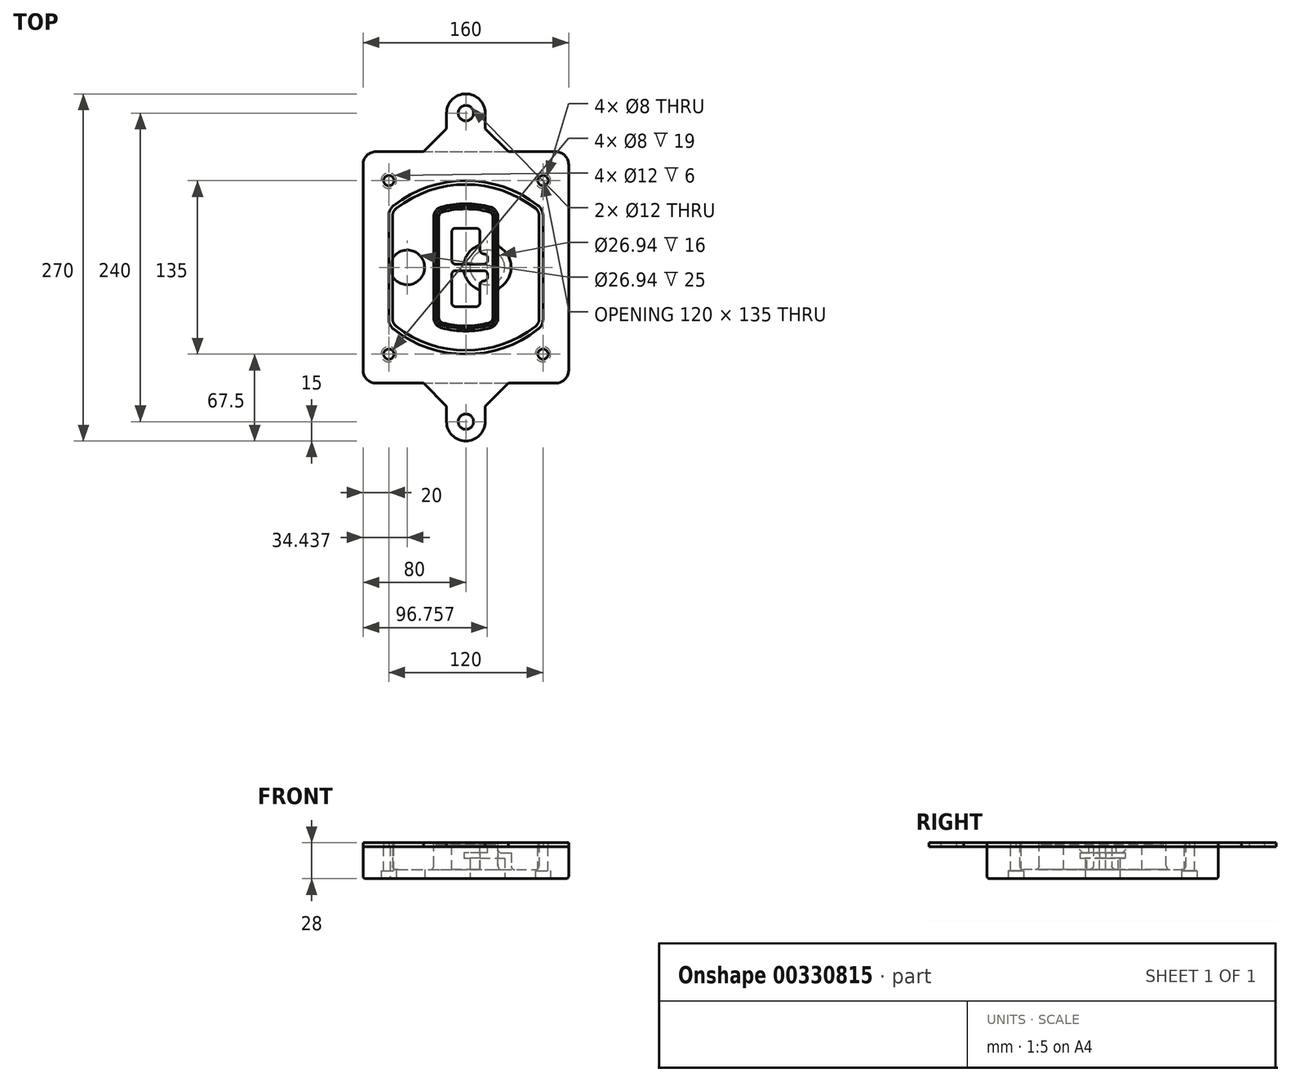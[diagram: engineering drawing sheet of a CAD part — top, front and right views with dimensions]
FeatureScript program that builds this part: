
annotation { "Feature Type Name" : "Feature", "Feature Type Description" : "" }
export const myFeature = defineFeature(function(context is Context, id is Id, definition is map)
    precondition{}
    {
        {
            var Q0;
            Q0=qCreatedBy(makeId("Top.planeOp"),FACE);
            var sketch = newSketch(context, id + "F0", { "sketchPlane" : qUnion([Q0])});
            skPoint(sketch, "E0.rect.middle", {"position": v(0, 0) * mm});
            skLineSegment(sketch, "E1.bottom", {"start": v(-70, -90) * mm, "end": v(70, -90) * mm});
            skLineSegment(sketch, "E1.top", {"start": v(-70, 90) * mm, "end": v(70, 90) * mm});
            skLineSegment(sketch, "E1.left", {"start": v(-80, -80) * mm, "end": v(-80, 80) * mm});
            skLineSegment(sketch, "E1.right", {"start": v(80, -80) * mm, "end": v(80, 80) * mm});
            skLineSegment(sketch, "E2", {"start": v(-80, 90) * mm, "end": v(80, -90) * mm, "construction": true});
            skLineSegment(sketch, "E3", {"start": v(80, 90) * mm, "end": v(-80, -90) * mm, "construction": true});
            skCircle(sketch, "E4", {"center": v(-60, 67.5) * mm, "radius": 4 * mm});
            skCircle(sketch, "E5", {"center": v(60, 67.5) * mm, "radius": 4 * mm});
            skCircle(sketch, "E6", {"center": v(60, -67.5) * mm, "radius": 4 * mm});
            skCircle(sketch, "E7", {"center": v(-60, -67.5) * mm, "radius": 4 * mm});
            skLineSegment(sketch, "E8", {"start": v(-60, 67.5) * mm, "end": v(60, 67.5) * mm, "construction": true});
            skLineSegment(sketch, "E9", {"start": v(60, 67.5) * mm, "end": v(60, -67.5) * mm, "construction": true});
            skLineSegment(sketch, "E10", {"start": v(60, -67.5) * mm, "end": v(-60, -67.5) * mm, "construction": true});
            skLineSegment(sketch, "E11", {"start": v(-60, -67.5) * mm, "end": v(-60, 67.5) * mm, "construction": true});
            skLineSegment(sketch, "E12", {"start": v(-60, 40.3) * mm, "end": v(-60, -40.3) * mm});
            skLineSegment(sketch, "E13", {"start": v(60, 40.3) * mm, "end": v(60, -40.3) * mm});
            skArc(sketch, "E14", {"start": v(56.15, 48.18) * mm, "mid": v(0, 67.5) * mm, "end": v(-56.15, 48.18) * mm});
            skArc(sketch, "E15", {"start": v(-56.15, -48.18) * mm, "mid": v(0, -67.5) * mm, "end": v(56.15, -48.18) * mm});
            skLineSegment(sketch, "E16", {"start": v(-60, 0) * mm, "end": v(60, 0) * mm, "construction": true});
            skPoint(sketch, "E17.visualSharp", {"position": v(-60, -45) * mm});
            skArc(sketch, "E17.filletArc", {"start": v(-60, -40.3) * mm, "mid": v(-58.99, -44.68) * mm, "end": v(-56.15, -48.18) * mm});
            skPoint(sketch, "E18.visualSharp", {"position": v(-60, 45) * mm});
            skArc(sketch, "E18.filletArc", {"start": v(-56.15, 48.18) * mm, "mid": v(-58.99, 44.68) * mm, "end": v(-60, 40.3) * mm});
            skPoint(sketch, "E19.visualSharp", {"position": v(60, 45) * mm});
            skArc(sketch, "E19.filletArc", {"start": v(60, 40.3) * mm, "mid": v(58.99, 44.68) * mm, "end": v(56.15, 48.18) * mm});
            skPoint(sketch, "E20.visualSharp", {"position": v(60, -45) * mm});
            skArc(sketch, "E20.filletArc", {"start": v(56.15, -48.18) * mm, "mid": v(58.99, -44.68) * mm, "end": v(60, -40.3) * mm});
            skPoint(sketch, "E21.visualSharp", {"position": v(-80, 90) * mm});
            skArc(sketch, "E21.filletArc", {"start": v(-70, 90) * mm, "mid": v(-77.07, 87.07) * mm, "end": v(-80, 80) * mm});
            skPoint(sketch, "E22.visualSharp", {"position": v(80, 90) * mm});
            skArc(sketch, "E22.filletArc", {"start": v(80, 80) * mm, "mid": v(77.07, 87.07) * mm, "end": v(70, 90) * mm});
            skPoint(sketch, "E23.visualSharp", {"position": v(80, -90) * mm});
            skArc(sketch, "E23.filletArc", {"start": v(70, -90) * mm, "mid": v(77.07, -87.07) * mm, "end": v(80, -80) * mm});
            skPoint(sketch, "E24.visualSharp", {"position": v(-80, -90) * mm});
            skArc(sketch, "E24.filletArc", {"start": v(-80, -80) * mm, "mid": v(-77.07, -87.07) * mm, "end": v(-70, -90) * mm});
            skArc(sketch, "E25.0", {"start": v(57, 40.3) * mm, "mid": v(56.3, 43.36) * mm, "end": v(54.3, 45.81) * mm});
            skLineSegment(sketch, "E25.1", {"start": v(57, 40.3) * mm, "end": v(57, -40.3) * mm});
            skArc(sketch, "E25.2", {"start": v(54.3, -45.81) * mm, "mid": v(56.3, -43.36) * mm, "end": v(57, -40.3) * mm});
            skArc(sketch, "E25.3", {"start": v(-54.3, -45.81) * mm, "mid": v(0, -64.5) * mm, "end": v(54.3, -45.81) * mm});
            skArc(sketch, "E25.4", {"start": v(-57, -40.3) * mm, "mid": v(-56.3, -43.36) * mm, "end": v(-54.3, -45.81) * mm});
            skArc(sketch, "E25.5", {"start": v(54.3, 45.81) * mm, "mid": v(0, 64.5) * mm, "end": v(-54.3, 45.81) * mm});
            skLineSegment(sketch, "E25.6", {"start": v(-57, 40.3) * mm, "end": v(-57, -40.3) * mm});
            skArc(sketch, "E25.7", {"start": v(-54.3, 45.81) * mm, "mid": v(-56.3, 43.36) * mm, "end": v(-57, 40.3) * mm});
            skArc(sketch, "E26.0", {"start": v(-58.62, 51.33) * mm, "mid": v(-62.58, 46.43) * mm, "end": v(-64, 40.3) * mm});
            skArc(sketch, "E26.1", {"start": v(58.62, 51.33) * mm, "mid": v(0, 71.5) * mm, "end": v(-58.62, 51.33) * mm});
            skArc(sketch, "E26.2", {"start": v(64, 40.3) * mm, "mid": v(62.58, 46.43) * mm, "end": v(58.62, 51.33) * mm});
            skLineSegment(sketch, "E26.3", {"start": v(64, 40.3) * mm, "end": v(64, -40.3) * mm});
            skArc(sketch, "E26.4", {"start": v(58.62, -51.33) * mm, "mid": v(62.58, -46.43) * mm, "end": v(64, -40.3) * mm});
            skLineSegment(sketch, "E26.5", {"start": v(-64, 40.3) * mm, "end": v(-64, -40.3) * mm});
            skArc(sketch, "E26.6", {"start": v(-58.62, -51.33) * mm, "mid": v(0, -71.5) * mm, "end": v(58.62, -51.33) * mm});
            skArc(sketch, "E26.7", {"start": v(-64, -40.3) * mm, "mid": v(-62.58, -46.43) * mm, "end": v(-58.62, -51.33) * mm});
            skSolve(sketch);
        }
        {
            var Q0;
            Q0=makeQuery(id+"F0.imprint","IMPRINT",FACE,{"disambiguationData":[TD([[makeQuery(id+"F0.imprint","IMPRINT",EDGE,{"derivedFrom":sQuery(id+"F0.wireOp",EDGE,"E1.bottom")}),1.0]])]});
            var Q1;
            Q1=makeQuery(id+"F0.imprint","IMPRINT",FACE,{"disambiguationData":[TD([[makeQuery(id+"F0.imprint","IMPRINT",EDGE,{"derivedFrom":sQuery(id+"F0.wireOp",EDGE,"E12")}),1.0]])]});
            var Q2;
            Q2=makeQuery(id+"F0.imprint","IMPRINT",FACE,{"disambiguationData":[TD([[makeQuery(id+"F0.imprint","IMPRINT",EDGE,{"derivedFrom":sQuery(id+"F0.wireOp",EDGE,"E25.0")}),1.0]])]});
            var Q3;
            Q3=makeQuery(id+"F0.imprint","IMPRINT",FACE,{"disambiguationData":[TD([[makeQuery(id+"F0.imprint","IMPRINT",EDGE,{"derivedFrom":sQuery(id+"F0.wireOp",EDGE,"E12")}),-1.0]])]});
            extrude(context, id + "F1", {"entities" : qUnion([Q0, Q1, Q2, Q3]), "oppositeDirection" : true, "depth" : 25 * mm});
        }
        {
            var Q0;
            Q0=makeQuery(id+"F0.imprint","IMPRINT",FACE,{"disambiguationData":[TD([[makeQuery(id+"F0.imprint","IMPRINT",EDGE,{"derivedFrom":sQuery(id+"F0.wireOp",EDGE,"E12")}),1.0]])]});
            extrude(context, id + "F2", {"entities" : qUnion([Q0]), "operationType" : NewBodyOperationType.ADD, "depth" : 3 * mm});
        }
        {
            var Q0;
            Q0=makeQuery(id+"F0.imprint","IMPRINT",FACE,{"disambiguationData":[TD([[makeQuery(id+"F0.imprint","IMPRINT",EDGE,{"derivedFrom":sQuery(id+"F0.wireOp",EDGE,"E25.0")}),1.0]])]});
            extrude(context, id + "F3", {"entities" : qUnion([Q0]), "operationType" : NewBodyOperationType.REMOVE, "oppositeDirection" : true, "depth" : 18 * mm});
        }
        {
            var Q0;
            Q0=makeQuery(id+"F2.opExtrude","CAP_FACE",FACE,{"disambiguationData":[OSD([sQuery(id+"F0.wireOp",EDGE,"E12"),sQuery(id+"F0.wireOp",EDGE,"E13"),sQuery(id+"F0.wireOp",EDGE,"E14"),sQuery(id+"F0.wireOp",EDGE,"E15"),sQuery(id+"F0.wireOp",EDGE,"E17.filletArc"),sQuery(id+"F0.wireOp",EDGE,"E18.filletArc"),sQuery(id+"F0.wireOp",EDGE,"E19.filletArc"),sQuery(id+"F0.wireOp",EDGE,"E20.filletArc"),sQuery(id+"F0.wireOp",EDGE,"E25.0"),sQuery(id+"F0.wireOp",EDGE,"E25.1"),sQuery(id+"F0.wireOp",EDGE,"E25.2"),sQuery(id+"F0.wireOp",EDGE,"E25.3"),sQuery(id+"F0.wireOp",EDGE,"E25.4"),sQuery(id+"F0.wireOp",EDGE,"E25.5"),sQuery(id+"F0.wireOp",EDGE,"E25.6"),sQuery(id+"F0.wireOp",EDGE,"E25.7")])],"isStart":false});
            var sketch = newSketch(context, id + "F4", { "sketchPlane" : qUnion([Q0])});
            skArc(sketch, "E27.0", {"start": v(-19.08, -46.97) * mm, "mid": v(0, -49.5) * mm, "end": v(19.08, -46.97) * mm});
            skArc(sketch, "E28.0", {"start": v(19.08, 46.97) * mm, "mid": v(0, 49.5) * mm, "end": v(-19.08, 46.97) * mm});
            skLineSegment(sketch, "E29", {"start": v(-25, 39.25) * mm, "end": v(-25, -39.25) * mm});
            skLineSegment(sketch, "E30", {"start": v(25, 39.25) * mm, "end": v(25, -39.25) * mm});
            skLineSegment(sketch, "E31", {"start": v(-25, 45.1) * mm, "end": v(25, 45.1) * mm, "construction": true});
            skLineSegment(sketch, "E32", {"start": v(-25, -45.1) * mm, "end": v(25, -45.1) * mm, "construction": true});
            skPoint(sketch, "E33.visualSharp", {"position": v(-25, 45.1) * mm});
            skArc(sketch, "E33.filletArc", {"start": v(-19.08, 46.97) * mm, "mid": v(-23.35, 44.11) * mm, "end": v(-25, 39.25) * mm});
            skPoint(sketch, "E34.visualSharp", {"position": v(25, 45.1) * mm});
            skArc(sketch, "E34.filletArc", {"start": v(25, 39.25) * mm, "mid": v(23.35, 44.11) * mm, "end": v(19.08, 46.97) * mm});
            skPoint(sketch, "E35.visualSharp", {"position": v(25, -45.1) * mm});
            skArc(sketch, "E35.filletArc", {"start": v(19.08, -46.97) * mm, "mid": v(23.35, -44.11) * mm, "end": v(25, -39.25) * mm});
            skPoint(sketch, "E36.visualSharp", {"position": v(-25, -45.1) * mm});
            skArc(sketch, "E36.filletArc", {"start": v(-25, -39.25) * mm, "mid": v(-23.35, -44.11) * mm, "end": v(-19.08, -46.97) * mm});
            skArc(sketch, "E37.0", {"start": v(54.3, 45.81) * mm, "mid": v(0, 64.5) * mm, "end": v(-54.3, 45.81) * mm});
            skArc(sketch, "E37.1", {"start": v(-54.3, 45.81) * mm, "mid": v(-56.3, 43.36) * mm, "end": v(-57, 40.3) * mm});
            skLineSegment(sketch, "E37.2", {"start": v(-57, 40.3) * mm, "end": v(-57, -40.3) * mm});
            skArc(sketch, "E37.3", {"start": v(-57, -40.3) * mm, "mid": v(-56.3, -43.36) * mm, "end": v(-54.3, -45.81) * mm});
            skArc(sketch, "E37.4", {"start": v(-54.3, -45.81) * mm, "mid": v(0, -64.5) * mm, "end": v(54.3, -45.81) * mm});
            skArc(sketch, "E37.5", {"start": v(54.3, -45.81) * mm, "mid": v(56.3, -43.36) * mm, "end": v(57, -40.3) * mm});
            skLineSegment(sketch, "E37.6", {"start": v(57, 40.3) * mm, "end": v(57, -40.3) * mm});
            skArc(sketch, "E37.7", {"start": v(57, 40.3) * mm, "mid": v(56.3, 43.36) * mm, "end": v(54.3, 45.81) * mm});
            skLineSegment(sketch, "E38.0", {"start": v(23, 39.25) * mm, "end": v(23, -39.25) * mm});
            skArc(sketch, "E38.1", {"start": v(18.56, -45.04) * mm, "mid": v(21.76, -42.9) * mm, "end": v(23, -39.25) * mm});
            skArc(sketch, "E38.2", {"start": v(-18.56, -45.04) * mm, "mid": v(0, -47.5) * mm, "end": v(18.56, -45.04) * mm});
            skArc(sketch, "E38.3", {"start": v(-23, -39.25) * mm, "mid": v(-21.76, -42.9) * mm, "end": v(-18.56, -45.04) * mm});
            skLineSegment(sketch, "E38.4", {"start": v(-23, 39.25) * mm, "end": v(-23, -39.25) * mm});
            skArc(sketch, "E38.5", {"start": v(23, 39.25) * mm, "mid": v(21.76, 42.9) * mm, "end": v(18.56, 45.04) * mm});
            skArc(sketch, "E38.6", {"start": v(-18.56, 45.04) * mm, "mid": v(-21.76, 42.9) * mm, "end": v(-23, 39.25) * mm});
            skArc(sketch, "E38.7", {"start": v(18.56, 45.04) * mm, "mid": v(0, 47.5) * mm, "end": v(-18.56, 45.04) * mm});
            skArc(sketch, "E39.0", {"start": v(21, 39.25) * mm, "mid": v(20.18, 41.68) * mm, "end": v(18.04, 43.1) * mm});
            skLineSegment(sketch, "E39.1", {"start": v(21, 39.25) * mm, "end": v(21, -39.25) * mm});
            skArc(sketch, "E39.2", {"start": v(18.04, -43.1) * mm, "mid": v(20.18, -41.68) * mm, "end": v(21, -39.25) * mm});
            skArc(sketch, "E39.3", {"start": v(-18.04, -43.1) * mm, "mid": v(0, -45.5) * mm, "end": v(18.04, -43.1) * mm});
            skArc(sketch, "E39.4", {"start": v(-21, -39.25) * mm, "mid": v(-20.18, -41.68) * mm, "end": v(-18.04, -43.1) * mm});
            skArc(sketch, "E39.5", {"start": v(18.04, 43.1) * mm, "mid": v(0, 45.5) * mm, "end": v(-18.04, 43.1) * mm});
            skLineSegment(sketch, "E39.6", {"start": v(-21, 39.25) * mm, "end": v(-21, -39.25) * mm});
            skArc(sketch, "E39.7", {"start": v(-18.04, 43.1) * mm, "mid": v(-20.18, 41.68) * mm, "end": v(-21, 39.25) * mm});
            skLineSegment(sketch, "E40", {"start": v(-25, 0) * mm, "end": v(25, 0) * mm, "construction": true});
            skLineSegment(sketch, "E41", {"start": v(-11, 5.5) * mm, "end": v(-11, 27.5) * mm});
            skLineSegment(sketch, "E42", {"start": v(-8, 30.5) * mm, "end": v(8, 30.5) * mm});
            skLineSegment(sketch, "E43", {"start": v(11, 27.5) * mm, "end": v(11, 13.5) * mm});
            skLineSegment(sketch, "E44", {"start": v(14, 10.5) * mm, "end": v(14, 10.5) * mm});
            skLineSegment(sketch, "E45", {"start": v(17, 7.5) * mm, "end": v(17, 5.5) * mm});
            skLineSegment(sketch, "E46", {"start": v(14, 2.5) * mm, "end": v(-8, 2.5) * mm});
            skPoint(sketch, "E47.visualSharp", {"position": v(-11, 30.5) * mm});
            skArc(sketch, "E47.filletArc", {"start": v(-8, 30.5) * mm, "mid": v(-10.12, 29.62) * mm, "end": v(-11, 27.5) * mm});
            skPoint(sketch, "E48.visualSharp", {"position": v(11, 30.5) * mm});
            skArc(sketch, "E48.filletArc", {"start": v(11, 27.5) * mm, "mid": v(10.12, 29.62) * mm, "end": v(8, 30.5) * mm});
            skPoint(sketch, "E49.visualSharp", {"position": v(11, 10.5) * mm});
            skArc(sketch, "E49.filletArc", {"start": v(11, 13.5) * mm, "mid": v(11.88, 11.38) * mm, "end": v(14, 10.5) * mm});
            skPoint(sketch, "E50.visualSharp", {"position": v(17, 10.5) * mm});
            skArc(sketch, "E50.filletArc", {"start": v(17, 7.5) * mm, "mid": v(16.12, 9.62) * mm, "end": v(14, 10.5) * mm});
            skPoint(sketch, "E51.visualSharp", {"position": v(17, 2.5) * mm});
            skArc(sketch, "E51.filletArc", {"start": v(14, 2.5) * mm, "mid": v(16.12, 3.38) * mm, "end": v(17, 5.5) * mm});
            skPoint(sketch, "E52.visualSharp", {"position": v(-11, 2.5) * mm});
            skArc(sketch, "E52.filletArc", {"start": v(-11, 5.5) * mm, "mid": v(-10.12, 3.38) * mm, "end": v(-8, 2.5) * mm});
            skLineSegment(sketch, "E53.0.MirrorCS", {"start": v(14, -2.5) * mm, "end": v(-8, -2.5) * mm});
            skArc(sketch, "E54.0.MirrorCS", {"start": v(-11, -5.5) * mm, "mid": v(-10.12, -3.38) * mm, "end": v(-8, -2.5) * mm});
            skLineSegment(sketch, "E55.0.MirrorCS", {"start": v(-11, -5.5) * mm, "end": v(-11, -27.5) * mm});
            skArc(sketch, "E56.0.MirrorCS", {"start": v(-8, -30.5) * mm, "mid": v(-10.12, -29.62) * mm, "end": v(-11, -27.5) * mm});
            skLineSegment(sketch, "E57.0.MirrorCS", {"start": v(-8, -30.5) * mm, "end": v(8, -30.5) * mm});
            skArc(sketch, "E58.0.MirrorCS", {"start": v(11, -27.5) * mm, "mid": v(10.12, -29.62) * mm, "end": v(8, -30.5) * mm});
            skLineSegment(sketch, "E59.0.MirrorCS", {"start": v(11, -27.5) * mm, "end": v(11, -13.5) * mm});
            skArc(sketch, "E60.0.MirrorCS", {"start": v(11, -13.5) * mm, "mid": v(11.88, -11.38) * mm, "end": v(14, -10.5) * mm});
            skArc(sketch, "E61.0.MirrorCS", {"start": v(17, -7.5) * mm, "mid": v(16.12, -9.62) * mm, "end": v(14, -10.5) * mm});
            skLineSegment(sketch, "E62.0.MirrorCS", {"start": v(17, -7.5) * mm, "end": v(17, -5.5) * mm});
            skArc(sketch, "E63.0.MirrorCS", {"start": v(14, -2.5) * mm, "mid": v(16.12, -3.38) * mm, "end": v(17, -5.5) * mm});
            skSolve(sketch);
        }
        {
            var Q0;
            Q0=makeQuery(id+"F4.imprint","IMPRINT",FACE,{"disambiguationData":[TD([[makeQuery(id+"F4.imprint","IMPRINT",EDGE,{"derivedFrom":sQuery(id+"F4.wireOp",EDGE,"E27.0")}),1.0]])]});
            var Q1;
            Q1=makeQuery(id+"F4.imprint","IMPRINT",FACE,{"disambiguationData":[TD([[makeQuery(id+"F4.imprint","IMPRINT",EDGE,{"derivedFrom":sQuery(id+"F4.wireOp",EDGE,"E38.0")}),-1.0]])]});
            var Q2;
            Q2=makeQuery(id+"F4.imprint","IMPRINT",FACE,{"disambiguationData":[TD([[makeQuery(id+"F4.imprint","IMPRINT",EDGE,{"derivedFrom":sQuery(id+"F4.wireOp",EDGE,"E39.0")}),1.0]])]});
            extrude(context, id + "F5", {"entities" : qUnion([Q0, Q1, Q2]), "operationType" : NewBodyOperationType.ADD, "endBound" : BoundingType.UP_TO_NEXT, "oppositeDirection" : true, "depth" : 25 * mm});
        }
        {
            var Q0;
            Q0=makeQuery(id+"F4.imprint","IMPRINT",FACE,{"disambiguationData":[TD([[makeQuery(id+"F4.imprint","IMPRINT",EDGE,{"derivedFrom":sQuery(id+"F4.wireOp",EDGE,"E38.0")}),-1.0]])]});
            extrude(context, id + "F6", {"entities" : qUnion([Q0]), "operationType" : NewBodyOperationType.REMOVE, "oppositeDirection" : true, "depth" : 2 * mm});
        }
        {
            var Q0;
            Q0=makeQuery(id+"F1.opExtrude","CAP_FACE",FACE,{"disambiguationData":[OSD([sQuery(id+"F0.wireOp",EDGE,"E1.bottom"),sQuery(id+"F0.wireOp",EDGE,"E1.top"),sQuery(id+"F0.wireOp",EDGE,"E1.left"),sQuery(id+"F0.wireOp",EDGE,"E1.right"),sQuery(id+"F0.wireOp",EDGE,"E4"),sQuery(id+"F0.wireOp",EDGE,"E5"),sQuery(id+"F0.wireOp",EDGE,"E6"),sQuery(id+"F0.wireOp",EDGE,"E7"),sQuery(id+"F0.wireOp",EDGE,"E21.filletArc"),sQuery(id+"F0.wireOp",EDGE,"E22.filletArc"),sQuery(id+"F0.wireOp",EDGE,"E23.filletArc"),sQuery(id+"F0.wireOp",EDGE,"E24.filletArc")])],"isStart":false});
            var sketch = newSketch(context, id + "F7", { "sketchPlane" : qUnion([Q0])});
            skCircle(sketch, "E64", {"center": v(16.76, 0) * mm, "radius": 13.47 * mm});
            skCircle(sketch, "E65", {"center": v(-45.56, 0) * mm, "radius": 13.47 * mm});
            skLineSegment(sketch, "E66", {"start": v(80, 0) * mm, "end": v(-80, 0) * mm});
            skCircle(sketch, "E67", {"center": v(16.76, 0) * mm, "radius": 18.47 * mm});
            skCircle(sketch, "E68", {"center": v(60, -67.5) * mm, "radius": 6 * mm});
            skCircle(sketch, "E69", {"center": v(-60, -67.5) * mm, "radius": 6 * mm});
            skCircle(sketch, "E70", {"center": v(-60, 67.5) * mm, "radius": 6 * mm});
            skCircle(sketch, "E71", {"center": v(60, 67.5) * mm, "radius": 6 * mm});
            skSolve(sketch);
        }
        {
            var Q0;
            {var subQ1=sQuery(id+"F7.wireOp",EDGE,"E66");var subQ4=sQuery(id+"F7.wireOp",EDGE,"E64");var subQ6=makeQuery(id+"F7.imprint","INTERSECT",VERTEX,{"disambiguationData":[OD(0.0)],"derivedFrom":[subQ4,subQ1]});Q0=makeQuery(id+"F7.imprint","IMPRINT",FACE,{"disambiguationData":[TD([[makeQuery(id+"F7.imprint","IMPRINT",EDGE,{"disambiguationData":[TD([[subQ6,-1.0]])],"derivedFrom":subQ4}),-1.0]])]});}
            var Q1;
            {var subQ0=sQuery(id+"F7.wireOp",EDGE,"E66");var subQ1=sQuery(id+"F7.wireOp",EDGE,"E64");var subQ3=makeQuery(id+"F7.imprint","INTERSECT",VERTEX,{"disambiguationData":[OD(0.0)],"derivedFrom":[subQ1,subQ0]});Q1=makeQuery(id+"F7.imprint","IMPRINT",FACE,{"disambiguationData":[TD([[makeQuery(id+"F7.imprint","IMPRINT",EDGE,{"disambiguationData":[TD([[subQ3,-1.0]])],"derivedFrom":subQ1}),1.0]])]});}
            var Q2;
            {var subQ0=sQuery(id+"F7.wireOp",EDGE,"E66");var subQ1=sQuery(id+"F7.wireOp",EDGE,"E64");var subQ3=makeQuery(id+"F7.imprint","INTERSECT",VERTEX,{"disambiguationData":[OD(0.0)],"derivedFrom":[subQ1,subQ0]});Q2=makeQuery(id+"F7.imprint","IMPRINT",FACE,{"disambiguationData":[TD([[makeQuery(id+"F7.imprint","IMPRINT",EDGE,{"disambiguationData":[TD([[subQ3,1.0]])],"derivedFrom":subQ1}),1.0]])]});}
            var Q3;
            {var subQ1=sQuery(id+"F7.wireOp",EDGE,"E66");var subQ4=sQuery(id+"F7.wireOp",EDGE,"E64");var subQ6=makeQuery(id+"F7.imprint","INTERSECT",VERTEX,{"disambiguationData":[OD(0.0)],"derivedFrom":[subQ4,subQ1]});Q3=makeQuery(id+"F7.imprint","IMPRINT",FACE,{"disambiguationData":[TD([[makeQuery(id+"F7.imprint","IMPRINT",EDGE,{"disambiguationData":[TD([[subQ6,1.0]])],"derivedFrom":subQ4}),-1.0]])]});}
            extrude(context, id + "F8", {"entities" : qUnion([Q0, Q1, Q2, Q3]), "operationType" : NewBodyOperationType.ADD, "oppositeDirection" : true, "depth" : 20 * mm});
        }
        {
            var Q0;
            {var subQ0=sQuery(id+"F7.wireOp",EDGE,"E66");var subQ1=sQuery(id+"F7.wireOp",EDGE,"E64");var subQ3=makeQuery(id+"F7.imprint","INTERSECT",VERTEX,{"disambiguationData":[OD(0.0)],"derivedFrom":[subQ1,subQ0]});Q0=makeQuery(id+"F7.imprint","IMPRINT",FACE,{"disambiguationData":[TD([[makeQuery(id+"F7.imprint","IMPRINT",EDGE,{"disambiguationData":[TD([[subQ3,-1.0]])],"derivedFrom":subQ1}),1.0]])]});}
            var Q1;
            {var subQ0=sQuery(id+"F7.wireOp",EDGE,"E66");var subQ1=sQuery(id+"F7.wireOp",EDGE,"E64");var subQ3=makeQuery(id+"F7.imprint","INTERSECT",VERTEX,{"disambiguationData":[OD(0.0)],"derivedFrom":[subQ1,subQ0]});Q1=makeQuery(id+"F7.imprint","IMPRINT",FACE,{"disambiguationData":[TD([[makeQuery(id+"F7.imprint","IMPRINT",EDGE,{"disambiguationData":[TD([[subQ3,1.0]])],"derivedFrom":subQ1}),1.0]])]});}
            extrude(context, id + "F9", {"entities" : qUnion([Q0, Q1]), "operationType" : NewBodyOperationType.REMOVE, "oppositeDirection" : true, "depth" : 16 * mm});
        }
        {
            var Q0;
            {var subQ0=sQuery(id+"F7.wireOp",EDGE,"E66");var subQ1=sQuery(id+"F7.wireOp",EDGE,"E65");var subQ3=makeQuery(id+"F7.imprint","INTERSECT",VERTEX,{"disambiguationData":[OD(0.0)],"derivedFrom":[subQ1,subQ0]});Q0=makeQuery(id+"F7.imprint","IMPRINT",FACE,{"disambiguationData":[TD([[makeQuery(id+"F7.imprint","IMPRINT",EDGE,{"disambiguationData":[TD([[subQ3,-1.0]])],"derivedFrom":subQ1}),1.0]])]});}
            var Q1;
            {var subQ0=sQuery(id+"F7.wireOp",EDGE,"E66");var subQ1=sQuery(id+"F7.wireOp",EDGE,"E65");var subQ3=makeQuery(id+"F7.imprint","INTERSECT",VERTEX,{"disambiguationData":[OD(0.0)],"derivedFrom":[subQ1,subQ0]});Q1=makeQuery(id+"F7.imprint","IMPRINT",FACE,{"disambiguationData":[TD([[makeQuery(id+"F7.imprint","IMPRINT",EDGE,{"disambiguationData":[TD([[subQ3,1.0]])],"derivedFrom":subQ1}),1.0]])]});}
            extrude(context, id + "F10", {"entities" : qUnion([Q0, Q1]), "operationType" : NewBodyOperationType.REMOVE, "oppositeDirection" : true, "depth" : 25 * mm});
        }
        {
            var Q0;
            Q0=makeQuery(id+"F7.imprint","IMPRINT",FACE,{"disambiguationData":[TD([[makeQuery(id+"F7.imprint","IMPRINT",EDGE,{"derivedFrom":sQuery(id+"F7.wireOp",EDGE,"E68")}),1.0]])]});
            var Q1;
            Q1=makeQuery(id+"F7.imprint","IMPRINT",FACE,{"disambiguationData":[TD([[makeQuery(id+"F7.imprint","IMPRINT",EDGE,{"derivedFrom":makeQuery(id+"F1.opExtrude","CAP_EDGE",EDGE,{"disambiguationData":[OSD([sQuery(id+"F0.wireOp",EDGE,"E5")])],"isStart":false})}),-1.0]])]});
            var Q2;
            Q2=makeQuery(id+"F7.imprint","IMPRINT",FACE,{"disambiguationData":[TD([[makeQuery(id+"F7.imprint","IMPRINT",EDGE,{"derivedFrom":sQuery(id+"F7.wireOp",EDGE,"E69")}),1.0]])]});
            var Q3;
            Q3=makeQuery(id+"F7.imprint","IMPRINT",FACE,{"disambiguationData":[TD([[makeQuery(id+"F7.imprint","IMPRINT",EDGE,{"derivedFrom":makeQuery(id+"F1.opExtrude","CAP_EDGE",EDGE,{"disambiguationData":[OSD([sQuery(id+"F0.wireOp",EDGE,"E4")])],"isStart":false})}),-1.0]])]});
            var Q4;
            Q4=makeQuery(id+"F7.imprint","IMPRINT",FACE,{"disambiguationData":[TD([[makeQuery(id+"F7.imprint","IMPRINT",EDGE,{"derivedFrom":sQuery(id+"F7.wireOp",EDGE,"E70")}),1.0]])]});
            var Q5;
            Q5=makeQuery(id+"F7.imprint","IMPRINT",FACE,{"disambiguationData":[TD([[makeQuery(id+"F7.imprint","IMPRINT",EDGE,{"derivedFrom":makeQuery(id+"F1.opExtrude","CAP_EDGE",EDGE,{"disambiguationData":[OSD([sQuery(id+"F0.wireOp",EDGE,"E7")])],"isStart":false})}),-1.0]])]});
            var Q6;
            Q6=makeQuery(id+"F7.imprint","IMPRINT",FACE,{"disambiguationData":[TD([[makeQuery(id+"F7.imprint","IMPRINT",EDGE,{"derivedFrom":sQuery(id+"F7.wireOp",EDGE,"E71")}),1.0]])]});
            var Q7;
            Q7=makeQuery(id+"F7.imprint","IMPRINT",FACE,{"disambiguationData":[TD([[makeQuery(id+"F7.imprint","IMPRINT",EDGE,{"derivedFrom":makeQuery(id+"F1.opExtrude","CAP_EDGE",EDGE,{"disambiguationData":[OSD([sQuery(id+"F0.wireOp",EDGE,"E6")])],"isStart":false})}),-1.0]])]});
            extrude(context, id + "F11", {"entities" : qUnion([Q0, Q1, Q2, Q3, Q4, Q5, Q6, Q7]), "operationType" : NewBodyOperationType.REMOVE, "oppositeDirection" : true, "depth" : 6 * mm});
        }
        {
            var Q0;
            Q0=makeQuery(id+"F9.boolean.opBoolean","COPY",FACE,{"derivedFrom":makeQuery(id+"F9.opExtrude","CAP_FACE",FACE,{"disambiguationData":[OSD([sQuery(id+"F7.wireOp",EDGE,"E64")])],"isStart":false})});
            var sketch = newSketch(context, id + "F12", { "sketchPlane" : qUnion([Q0])});
            skArc(sketch, "E72.0", {"start": v(11, 17.55) * mm, "mid": v(2.57, 11.82) * mm, "end": v(-1.54, 2.5) * mm});
            skArc(sketch, "E72.1", {"start": v(-1.54, -2.5) * mm, "mid": v(2.57, -11.82) * mm, "end": v(11, -17.55) * mm});
            skLineSegment(sketch, "E73", {"start": v(-1.54, -2.5) * mm, "end": v(14, -2.5) * mm});
            skLineSegment(sketch, "E74.0", {"start": v(14, 2.5) * mm, "end": v(-1.54, 2.5) * mm});
            skArc(sketch, "E74.1", {"start": v(14, 2.5) * mm, "mid": v(16.12, 3.38) * mm, "end": v(17, 5.5) * mm});
            skLineSegment(sketch, "E74.2", {"start": v(17, 7.5) * mm, "end": v(17, 5.5) * mm});
            skArc(sketch, "E74.3", {"start": v(17, 7.5) * mm, "mid": v(16.12, 9.62) * mm, "end": v(14, 10.5) * mm});
            skArc(sketch, "E74.4", {"start": v(11, 13.5) * mm, "mid": v(11.88, 11.38) * mm, "end": v(14, 10.5) * mm});
            skLineSegment(sketch, "E74.5", {"start": v(11, 17.55) * mm, "end": v(11, 13.5) * mm});
            skLineSegment(sketch, "E74.7", {"start": v(14, -2.5) * mm, "end": v(-1.54, -2.5) * mm});
            skArc(sketch, "E74.8", {"start": v(14, -2.5) * mm, "mid": v(16.12, -3.38) * mm, "end": v(17, -5.5) * mm});
            skLineSegment(sketch, "E74.9", {"start": v(17, -7.5) * mm, "end": v(17, -5.5) * mm});
            skArc(sketch, "E74.10", {"start": v(17, -7.5) * mm, "mid": v(16.12, -9.62) * mm, "end": v(14, -10.5) * mm});
            skArc(sketch, "E74.11", {"start": v(11, -13.5) * mm, "mid": v(11.88, -11.38) * mm, "end": v(14, -10.5) * mm});
            skLineSegment(sketch, "E74.12", {"start": v(11, -17.55) * mm, "end": v(11, -13.5) * mm});
            skPoint(sketch, "E75.orphan", {"position": v(11, -27.5) * mm});
            skPoint(sketch, "E76.orphan", {"position": v(-8, -2.5) * mm});
            skPoint(sketch, "E77.orphan", {"position": v(-8, 2.5) * mm});
            skPoint(sketch, "E78.orphan", {"position": v(11, 27.5) * mm});
            skSolve(sketch);
        }
        {
            var Q0;
            {var subQ7=sQuery(id+"F12.wireOp",EDGE,"E72.0");var subQ14=sQuery(id+"F12.wireOp",EDGE,"E72.1");var subQ16=sQuery(id+"F12.wireOp",EDGE,"E74.1");var subQ18=sQuery(id+"F12.wireOp",EDGE,"E74.8");Q0=qUnion([makeQuery(id+"F12.imprint","IMPRINT",FACE,{"disambiguationData":[TD([[makeQuery(id+"F12.imprint","IMPRINT",EDGE,{"derivedFrom":subQ7}),1.0]])]}),makeQuery(id+"F12.imprint","IMPRINT",FACE,{"disambiguationData":[TD([[makeQuery(id+"F12.imprint","IMPRINT",EDGE,{"derivedFrom":subQ14}),1.0]])]}),makeQuery(id+"F12.imprint","IMPRINT",FACE,{"disambiguationData":[TD([[makeQuery(id+"F12.imprint","IMPRINT",EDGE,{"derivedFrom":subQ16}),1.0]])]}),makeQuery(id+"F12.imprint","IMPRINT",FACE,{"disambiguationData":[TD([[makeQuery(id+"F12.imprint","IMPRINT",EDGE,{"derivedFrom":subQ18}),-1.0]])]})]);}
            var Q1;
            Q1=makeQuery(id+"F5.boolean.opBoolean","SPLIT",FACE,{"disambiguationData":[TD([makeQuery(id+"F5.opExtrude","SWEPT_FACE",FACE,{"disambiguationData":[OSD([sQuery(id+"F4.wireOp",EDGE,"E41")])]})])],"derivedFrom":makeQuery(id+"F3.boolean.opBoolean","COPY",FACE,{"derivedFrom":makeQuery(id+"F3.opExtrude","CAP_FACE",FACE,{"disambiguationData":[OSD([sQuery(id+"F0.wireOp",EDGE,"E25.0"),sQuery(id+"F0.wireOp",EDGE,"E25.1"),sQuery(id+"F0.wireOp",EDGE,"E25.2"),sQuery(id+"F0.wireOp",EDGE,"E25.3"),sQuery(id+"F0.wireOp",EDGE,"E25.4"),sQuery(id+"F0.wireOp",EDGE,"E25.5"),sQuery(id+"F0.wireOp",EDGE,"E25.6"),sQuery(id+"F0.wireOp",EDGE,"E25.7")])],"isStart":false})})});
            extrude(context, id + "F13", {"entities" : qUnion([Q0]), "operationType" : NewBodyOperationType.REMOVE, "endBound" : BoundingType.UP_TO_SURFACE, "endBoundEntityFace" : qUnion([Q1]), "depth" : 25 * mm});
        }
        {
            var Q0;
            Q0=makeQuery(id+"F3.boolean.opBoolean","COPY",EDGE,{"derivedFrom":makeQuery(id+"F3.opExtrude","CAP_EDGE",EDGE,{"disambiguationData":[OSD([sQuery(id+"F0.wireOp",EDGE,"E25.6")])],"isStart":false})});
            var Q1;
            Q1=makeQuery(id+"F8.boolean.opBoolean","INTERSECT",EDGE,{"derivedFrom":[makeQuery(id+"F5.opExtrude","SWEPT_FACE",FACE,{"disambiguationData":[OSD([sQuery(id+"F4.wireOp",EDGE,"E30")])]}),makeQuery(id+"F8.opExtrude","CAP_FACE",FACE,{"disambiguationData":[OSD([sQuery(id+"F7.wireOp",EDGE,"E67")])],"isStart":false})]});
            var Q2;
            Q2=makeQuery(id+"F8.boolean.opBoolean","INTERSECT",EDGE,{"disambiguationData":[OD(1.0)],"derivedFrom":[makeQuery(id+"F5.opExtrude","SWEPT_FACE",FACE,{"disambiguationData":[OSD([sQuery(id+"F4.wireOp",EDGE,"E30")])]}),makeQuery(id+"F8.opExtrude","SWEPT_FACE",FACE,{"disambiguationData":[OSD([sQuery(id+"F7.wireOp",EDGE,"E67")])]})]});
            var Q3;
            {var subQ0=sQuery(id+"F4.wireOp",EDGE,"E30");Q3=makeQuery(id+"F8.boolean.opBoolean","SPLIT",EDGE,{"disambiguationData":[TD([makeQuery(id+"F5.opExtrude","SWEPT_FACE",FACE,{"disambiguationData":[OSD([sQuery(id+"F4.wireOp",EDGE,"E35.filletArc")])]})])],"derivedFrom":makeQuery(id+"F5.opExtrude","CAP_EDGE",EDGE,{"disambiguationData":[OSD([subQ0])],"isStart":false})});}
            var Q4;
            {var subQ0=sQuery(id+"F0.wireOp",EDGE,"E25.7");var subQ1=sQuery(id+"F0.wireOp",EDGE,"E25.1");var subQ2=sQuery(id+"F0.wireOp",EDGE,"E25.6");var subQ3=sQuery(id+"F0.wireOp",EDGE,"E25.5");var subQ4=sQuery(id+"F0.wireOp",EDGE,"E25.4");var subQ5=sQuery(id+"F0.wireOp",EDGE,"E25.0");var subQ6=sQuery(id+"F0.wireOp",EDGE,"E25.2");var subQ7=sQuery(id+"F0.wireOp",EDGE,"E25.3");Q4=makeQuery(id+"F8.boolean.opBoolean","INTERSECT",EDGE,{"derivedFrom":[makeQuery(id+"F5.boolean.opBoolean","SPLIT",FACE,{"disambiguationData":[TD([makeQuery(id+"F2.opExtrude","SWEPT_FACE",FACE,{"disambiguationData":[OSD([subQ5])]})])],"derivedFrom":makeQuery(id+"F3.boolean.opBoolean","COPY",FACE,{"derivedFrom":makeQuery(id+"F3.opExtrude","CAP_FACE",FACE,{"disambiguationData":[OSD([subQ5,subQ1,subQ6,subQ7,subQ4,subQ3,subQ2,subQ0])],"isStart":false})})}),makeQuery(id+"F8.opExtrude","SWEPT_FACE",FACE,{"disambiguationData":[OSD([sQuery(id+"F7.wireOp",EDGE,"E67")])]})]});}
            var Q5;
            Q5=makeQuery(id+"F8.boolean.opBoolean","INTERSECT",EDGE,{"disambiguationData":[OD(0.0)],"derivedFrom":[makeQuery(id+"F5.opExtrude","SWEPT_FACE",FACE,{"disambiguationData":[OSD([sQuery(id+"F4.wireOp",EDGE,"E30")])]}),makeQuery(id+"F8.opExtrude","SWEPT_FACE",FACE,{"disambiguationData":[OSD([sQuery(id+"F7.wireOp",EDGE,"E67")])]})]});
            fillet(context, id + "F14", {"entities" : qUnion([Q0, Q1, Q2, Q3, Q4, Q5]), "radius" : 3 * mm, "tangentPropagation" : true, "allowEdgeOverflow" : false});
        }
        {
            var Q0;
            Q0=makeQuery(id+"F1.opExtrude","CAP_EDGE",EDGE,{"disambiguationData":[OSD([sQuery(id+"F0.wireOp",EDGE,"E1.bottom")])],"isStart":false});
            fillet(context, id + "F15", {"entities" : qUnion([Q0]), "radius" : 2 * mm, "tangentPropagation" : true, "allowEdgeOverflow" : false});
        }
        {
            var Q0;
            {var subQ0=sQuery(id+"F0.wireOp",EDGE,"E21.filletArc");var subQ1=sQuery(id+"F0.wireOp",EDGE,"E7");var subQ2=sQuery(id+"F0.wireOp",EDGE,"E6");var subQ3=sQuery(id+"F0.wireOp",EDGE,"E5");var subQ4=sQuery(id+"F0.wireOp",EDGE,"E4");var subQ5=sQuery(id+"F0.wireOp",EDGE,"E22.filletArc");var subQ6=sQuery(id+"F0.wireOp",EDGE,"E1.bottom");var subQ7=sQuery(id+"F0.wireOp",EDGE,"E1.right");var subQ8=sQuery(id+"F0.wireOp",EDGE,"E1.top");var subQ9=sQuery(id+"F0.wireOp",EDGE,"E1.left");var subQ10=sQuery(id+"F0.wireOp",EDGE,"E23.filletArc");var subQ11=sQuery(id+"F0.wireOp",EDGE,"E24.filletArc");Q0=makeQuery(id+"F2.boolean.opBoolean","SPLIT",FACE,{"disambiguationData":[TD([makeQuery(id+"F1.opExtrude","SWEPT_FACE",FACE,{"disambiguationData":[OSD([subQ6])]})])],"derivedFrom":makeQuery(id+"F1.opExtrude","CAP_FACE",FACE,{"disambiguationData":[OSD([subQ6,subQ8,subQ9,subQ7,subQ4,subQ3,subQ2,subQ1,subQ0,subQ5,subQ10,subQ11])],"isStart":true})});}
            var sketch = newSketch(context, id + "F16", { "sketchPlane" : qUnion([Q0])});
            skLineSegment(sketch, "E79", {"start": v(0, 90) * mm, "end": v(0, 120) * mm, "construction": true});
            skCircle(sketch, "E80", {"center": v(0, 120) * mm, "radius": 6 * mm});
            skLineSegment(sketch, "E81", {"start": v(-33, 90) * mm, "end": v(-15, 108) * mm});
            skLineSegment(sketch, "E82", {"start": v(33, 90) * mm, "end": v(15, 108) * mm});
            skLineSegment(sketch, "E83", {"start": v(-15, 108) * mm, "end": v(-15, 120) * mm});
            skLineSegment(sketch, "E84", {"start": v(15, 108) * mm, "end": v(15, 120) * mm});
            skArc(sketch, "E85", {"start": v(15, 120) * mm, "mid": v(0, 135) * mm, "end": v(-15, 120) * mm});
            skLineSegment(sketch, "E86", {"start": v(-80, 0) * mm, "end": v(80, 0) * mm, "construction": true});
            skLineSegment(sketch, "E87.MirrorCS", {"start": v(33, -90) * mm, "end": v(15, -108) * mm});
            skLineSegment(sketch, "E88.MirrorCS", {"start": v(15, -108) * mm, "end": v(15, -120) * mm});
            skArc(sketch, "E89.MirrorCS", {"start": v(15, -120) * mm, "mid": v(0, -135) * mm, "end": v(-15, -120) * mm});
            skCircle(sketch, "E90.MirrorC", {"center": v(0, -120) * mm, "radius": 6 * mm});
            skLineSegment(sketch, "E91.MirrorCS", {"start": v(-15, -108) * mm, "end": v(-15, -120) * mm});
            skLineSegment(sketch, "E92.MirrorCS", {"start": v(-33, -90) * mm, "end": v(-15, -108) * mm});
            skLineSegment(sketch, "E93.MirrorCS", {"start": v(0, -90) * mm, "end": v(0, -120) * mm, "construction": true});
            skSolve(sketch);
        }
        {
            var Q0;
            Q0=makeQuery(id+"F16.imprint","IMPRINT",FACE,{"disambiguationData":[TD([[makeQuery(id+"F16.imprint","IMPRINT",EDGE,{"derivedFrom":makeQuery(id+"F1.opExtrude","CAP_EDGE",EDGE,{"disambiguationData":[OSD([sQuery(id+"F0.wireOp",EDGE,"E1.left")])],"isStart":true})}),-1.0]])]});
            var Q1;
            Q1=makeQuery(id+"F16.imprint","IMPRINT",FACE,{"disambiguationData":[TD([[makeQuery(id+"F16.imprint","IMPRINT",EDGE,{"derivedFrom":sQuery(id+"F16.wireOp",EDGE,"E80")}),-1.0]])]});
            var Q2;
            {var subQ0=sQuery(id+"F16.wireOp",EDGE,"E87.MirrorCS");Q2=makeQuery(id+"F16.imprint","IMPRINT",FACE,{"disambiguationData":[TD([[makeQuery(id+"F16.imprint","IMPRINT",EDGE,{"derivedFrom":subQ0}),-1.0]])]});}
            var Q3;
            Q3=makeQuery(id+"F2.opExtrude","CAP_FACE",FACE,{"disambiguationData":[OSD([sQuery(id+"F0.wireOp",EDGE,"E12"),sQuery(id+"F0.wireOp",EDGE,"E13"),sQuery(id+"F0.wireOp",EDGE,"E14"),sQuery(id+"F0.wireOp",EDGE,"E15"),sQuery(id+"F0.wireOp",EDGE,"E17.filletArc"),sQuery(id+"F0.wireOp",EDGE,"E18.filletArc"),sQuery(id+"F0.wireOp",EDGE,"E19.filletArc"),sQuery(id+"F0.wireOp",EDGE,"E20.filletArc"),sQuery(id+"F0.wireOp",EDGE,"E25.0"),sQuery(id+"F0.wireOp",EDGE,"E25.1"),sQuery(id+"F0.wireOp",EDGE,"E25.2"),sQuery(id+"F0.wireOp",EDGE,"E25.3"),sQuery(id+"F0.wireOp",EDGE,"E25.4"),sQuery(id+"F0.wireOp",EDGE,"E25.5"),sQuery(id+"F0.wireOp",EDGE,"E25.6"),sQuery(id+"F0.wireOp",EDGE,"E25.7")])],"isStart":false});
            extrude(context, id + "F17", {"entities" : qUnion([Q0, Q1, Q2]), "endBound" : BoundingType.UP_TO_SURFACE, "endBoundEntityFace" : qUnion([Q3]), "depth" : 25 * mm});
        }
    });
